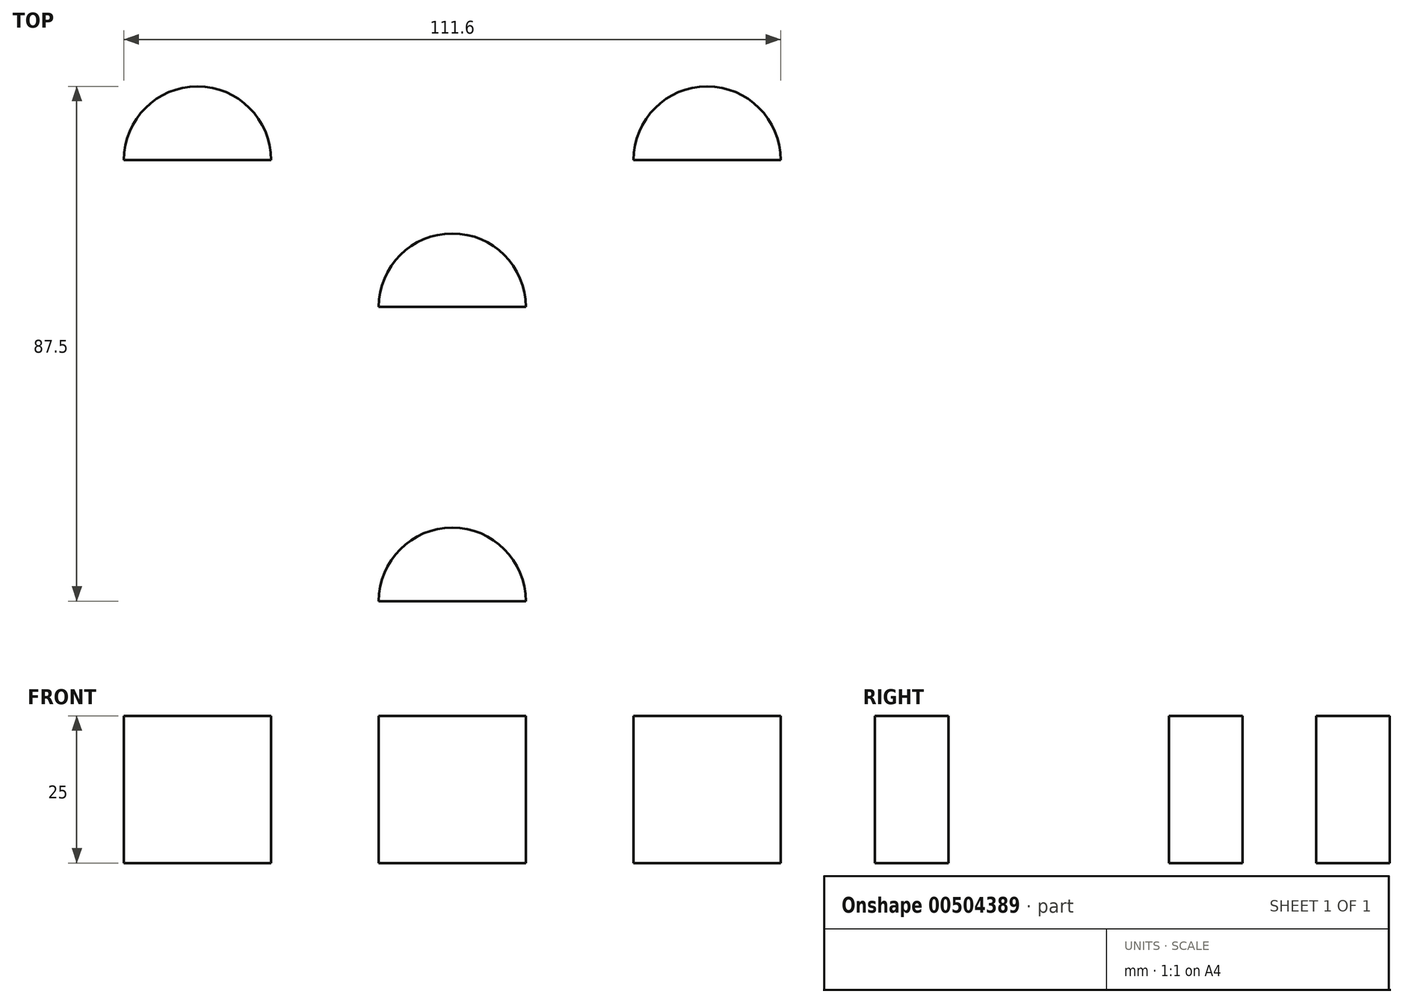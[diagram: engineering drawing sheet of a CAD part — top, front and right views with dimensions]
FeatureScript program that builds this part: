
annotation { "Feature Type Name" : "Feature", "Feature Type Description" : "" }
export const myFeature = defineFeature(function(context is Context, id is Id, definition is map)
    precondition{}
    {
        {
            var Q0;
            Q0=qCreatedBy(makeId("Top.planeOp"),FACE);
            var sketch = newSketch(context, id + "F0", { "sketchPlane" : qUnion([Q0])});
            skLineSegment(sketch, "E0.0", {"start": v(0, 25) * mm, "end": v(0, 25) * mm});
            skLineSegment(sketch, "E0.1", {"start": v(21.65, -12.5) * mm, "end": v(21.65, -12.5) * mm});
            skLineSegment(sketch, "E0.2", {"start": v(-21.65, -12.5) * mm, "end": v(-21.65, -12.5) * mm});
            skPoint(sketch, "E0.0.midPoint", {"position": v(0, 25) * mm});
            skArc(sketch, "E1", {"start": v(-21.65, 37.5) * mm, "mid": v(-64.95, 37.5) * mm, "end": v(-43.3, 0) * mm});
            skArc(sketch, "E2", {"start": v(43.3, 0) * mm, "mid": v(64.95, 37.5) * mm, "end": v(21.65, 37.5) * mm});
            skArc(sketch, "E3", {"start": v(-21.65, -37.5) * mm, "mid": v(0, -75) * mm, "end": v(21.65, -37.5) * mm});
            skPoint(sketch, "E0.cCircle.center.orphan", {"position": v(0, 0) * mm});
            skPoint(sketch, "E4.visualSharp", {"position": v(-30.8, 3.35) * mm});
            skArc(sketch, "E4.filletArc", {"start": v(-21.65, -12.5) * mm, "mid": v(-30.8, -3.35) * mm, "end": v(-43.3, 0) * mm});
            skPoint(sketch, "E5.visualSharp", {"position": v(-12.5, -28.35) * mm});
            skArc(sketch, "E5.filletArc", {"start": v(-21.65, -37.5) * mm, "mid": v(-18.3, -25) * mm, "end": v(-21.65, -12.5) * mm});
            skPoint(sketch, "E6.visualSharp", {"position": v(12.5, -28.35) * mm});
            skArc(sketch, "E6.filletArc", {"start": v(21.65, -12.5) * mm, "mid": v(18.3, -25) * mm, "end": v(21.65, -37.5) * mm});
            skPoint(sketch, "E7.visualSharp", {"position": v(30.8, 3.35) * mm});
            skArc(sketch, "E7.filletArc", {"start": v(43.3, 0) * mm, "mid": v(30.8, -3.35) * mm, "end": v(21.65, -12.5) * mm});
            skPoint(sketch, "E8.visualSharp", {"position": v(-18.3, 25) * mm});
            skArc(sketch, "E8.filletArc", {"start": v(-21.65, 37.5) * mm, "mid": v(-12.5, 28.35) * mm, "end": v(0, 25) * mm});
            skPoint(sketch, "E9.visualSharp", {"position": v(18.3, 25) * mm});
            skArc(sketch, "E9.filletArc", {"start": v(0, 25) * mm, "mid": v(12.5, 28.35) * mm, "end": v(21.65, 37.5) * mm});
            skCircle(sketch, "E10", {"center": v(-43.3, 25) * mm, "radius": 12.5 * mm});
            skCircle(sketch, "E11", {"center": v(43.3, 25) * mm, "radius": 12.5 * mm});
            skCircle(sketch, "E12", {"center": v(0, -50) * mm, "radius": 12.5 * mm});
            skCircle(sketch, "E13", {"center": v(0, 0) * mm, "radius": 12.5 * mm});
            skLineSegment(sketch, "E14", {"start": v(-55.8, 25) * mm, "end": v(-30.8, 25) * mm});
            skLineSegment(sketch, "E15", {"start": v(30.8, 25) * mm, "end": v(55.8, 25) * mm});
            skLineSegment(sketch, "E16", {"start": v(-12.5, -50) * mm, "end": v(12.5, -50) * mm});
            skLineSegment(sketch, "E17", {"start": v(-12.5, 0) * mm, "end": v(12.5, 0) * mm});
            skSolve(sketch);
        }
        {
            var Q0;
            {var subQ0=sQuery(id+"F0.wireOp",EDGE,"E14");Q0=makeQuery(id+"F0.imprint","IMPRINT",FACE,{"disambiguationData":[TD([[makeQuery(id+"F0.imprint","IMPRINT",EDGE,{"derivedFrom":subQ0}),1.0]])]});}
            var Q1;
            {var subQ0=sQuery(id+"F0.wireOp",EDGE,"E17");Q1=makeQuery(id+"F0.imprint","IMPRINT",FACE,{"disambiguationData":[TD([[makeQuery(id+"F0.imprint","IMPRINT",EDGE,{"derivedFrom":subQ0}),1.0]])]});}
            var Q2;
            {var subQ0=sQuery(id+"F0.wireOp",EDGE,"E15");Q2=makeQuery(id+"F0.imprint","IMPRINT",FACE,{"disambiguationData":[TD([[makeQuery(id+"F0.imprint","IMPRINT",EDGE,{"derivedFrom":subQ0}),1.0]])]});}
            var Q3;
            {var subQ0=sQuery(id+"F0.wireOp",EDGE,"E16");Q3=makeQuery(id+"F0.imprint","IMPRINT",FACE,{"disambiguationData":[TD([[makeQuery(id+"F0.imprint","IMPRINT",EDGE,{"derivedFrom":subQ0}),1.0]])]});}
            extrude(context, id + "F1", {"entities" : qUnion([Q0, Q1, Q2, Q3]), "depth" : 25 * mm, "offsetDistance" : 25 * mm});
        }
    });
